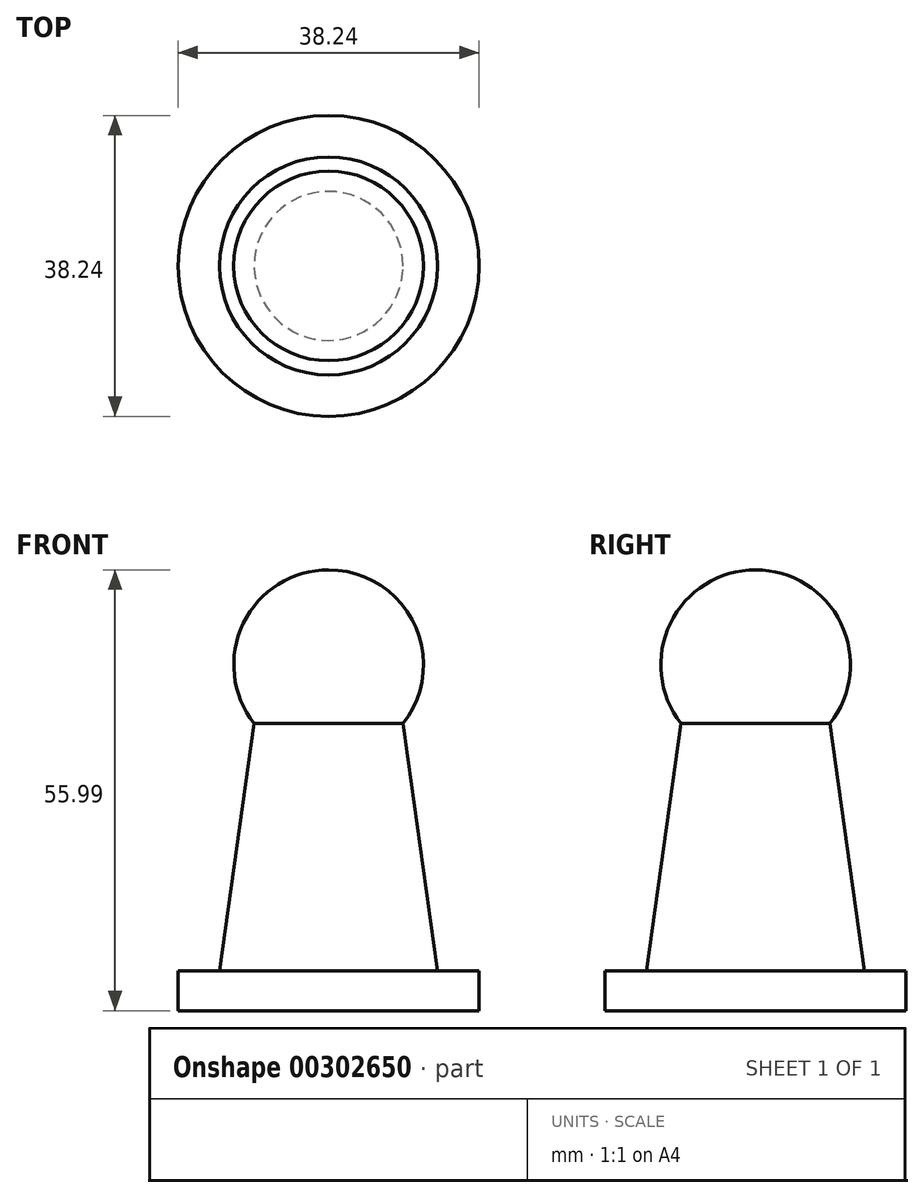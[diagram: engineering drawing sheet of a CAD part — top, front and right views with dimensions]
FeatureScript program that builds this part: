
annotation { "Feature Type Name" : "Feature", "Feature Type Description" : "" }
export const myFeature = defineFeature(function(context is Context, id is Id, definition is map)
    precondition{}
    {
        {
            var Q0;
            Q0=qCreatedBy(makeId("Front.planeOp"),FACE);
            var sketch = newSketch(context, id + "F0", { "sketchPlane" : qUnion([Q0])});
            skLineSegment(sketch, "E0", {"start": v(0, 0) * mm, "end": v(-19.12, 0) * mm});
            skLineSegment(sketch, "E1", {"start": v(-19.12, 0) * mm, "end": v(-19.12, 5.04) * mm});
            skLineSegment(sketch, "E2", {"start": v(-19.12, 5.04) * mm, "end": v(0, 5.04) * mm});
            skLineSegment(sketch, "E3", {"start": v(-13.85, 5.04) * mm, "end": v(-9.46, 36.5) * mm});
            skArc(sketch, "E4", {"start": v(0, 56) * mm, "mid": v(-12.05, 43.95) * mm, "end": v(0, 31.9) * mm});
            skLineSegment(sketch, "E5", {"start": v(0, 56) * mm, "end": v(0, 0) * mm});
            skSolve(sketch);
        }
        {
            var Q0;
            {var subQ3=sQuery(id+"F0.wireOp",EDGE,"E3");Q0=makeQuery(id+"F0.imprint","IMPRINT",FACE,{"disambiguationData":[TD([[makeQuery(id+"F0.imprint","IMPRINT",EDGE,{"derivedFrom":subQ3}),-1.0]])]});}
            var Q1;
            {var subQ5=sQuery(id+"F0.wireOp",EDGE,"E0");Q1=makeQuery(id+"F0.imprint","IMPRINT",FACE,{"disambiguationData":[TD([[makeQuery(id+"F0.imprint","IMPRINT",EDGE,{"derivedFrom":subQ5}),-1.0]])]});}
            var Q2;
            {var subQ0=sQuery(id+"F0.wireOp",EDGE,"E4");var subQ1=makeQuery(id+"F0.imprint","INTERSECT",VERTEX,{"derivedFrom":[sQuery(id+"F0.wireOp",EDGE,"E3"),subQ0]});Q2=makeQuery(id+"F0.imprint","IMPRINT",FACE,{"disambiguationData":[TD([[makeQuery(id+"F0.imprint","IMPRINT",EDGE,{"disambiguationData":[TD([[subQ1,1.0]])],"derivedFrom":subQ0}),1.0]])]});}
            var Q3;
            Q3=sQuery(id+"F0.wireOp",EDGE,"E5");
            revolve(context, id + "F1", {"entities" : qUnion([Q0, Q1, Q2]), "axis" : qUnion([Q3]), "revolveType" : RevolveType.FULL});
        }
    });
